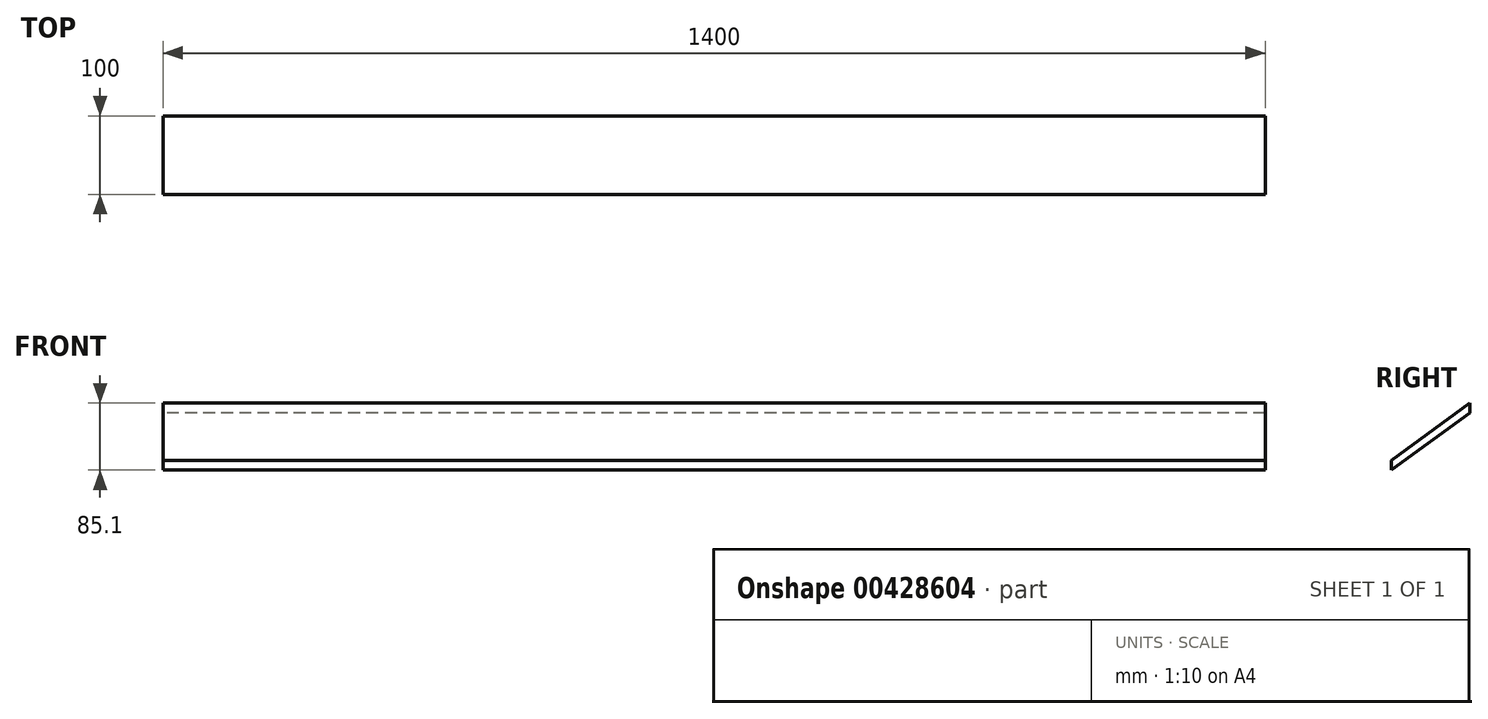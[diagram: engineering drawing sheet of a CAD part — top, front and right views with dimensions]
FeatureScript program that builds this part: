
annotation { "Feature Type Name" : "Feature", "Feature Type Description" : "" }
export const myFeature = defineFeature(function(context is Context, id is Id, definition is map)
    precondition{}
    {
        {
            var Q0;
            Q0=qCreatedBy(makeId("Right.planeOp"),FACE);
            var sketch = newSketch(context, id + "F0", { "sketchPlane" : qUnion([Q0])});
            skLineSegment(sketch, "E0", {"start": v(-26.2, 11.96) * mm, "end": v(73.8, 69.7) * mm, "construction": true});
            skLineSegment(sketch, "E1", {"start": v(-26.2, 11.96) * mm, "end": v(-26.2, -3.04) * mm, "construction": true});
            skLineSegment(sketch, "E2", {"start": v(73.8, 69.7) * mm, "end": v(-26.2, -3.04) * mm});
            skLineSegment(sketch, "E3", {"start": v(-26.2, -15.4) * mm, "end": v(73.8, 57.33) * mm});
            skLineSegment(sketch, "E4", {"start": v(73.8, 57.33) * mm, "end": v(73.8, 69.7) * mm});
            skLineSegment(sketch, "E5", {"start": v(-26.2, -15.4) * mm, "end": v(-26.2, -3.04) * mm});
            skSolve(sketch);
        }
        {
            var Q0;
            Q0=makeQuery(id+"F0.imprint","IMPRINT",FACE,{"disambiguationData":[TD([[makeQuery(id+"F0.imprint","IMPRINT",EDGE,{"derivedFrom":sQuery(id+"F0.wireOp",EDGE,"E2")}),1.0]])]});
            extrude(context, id + "F1", {"entities" : qUnion([Q0]), "depth" : 1400 * mm});
        }
    });
